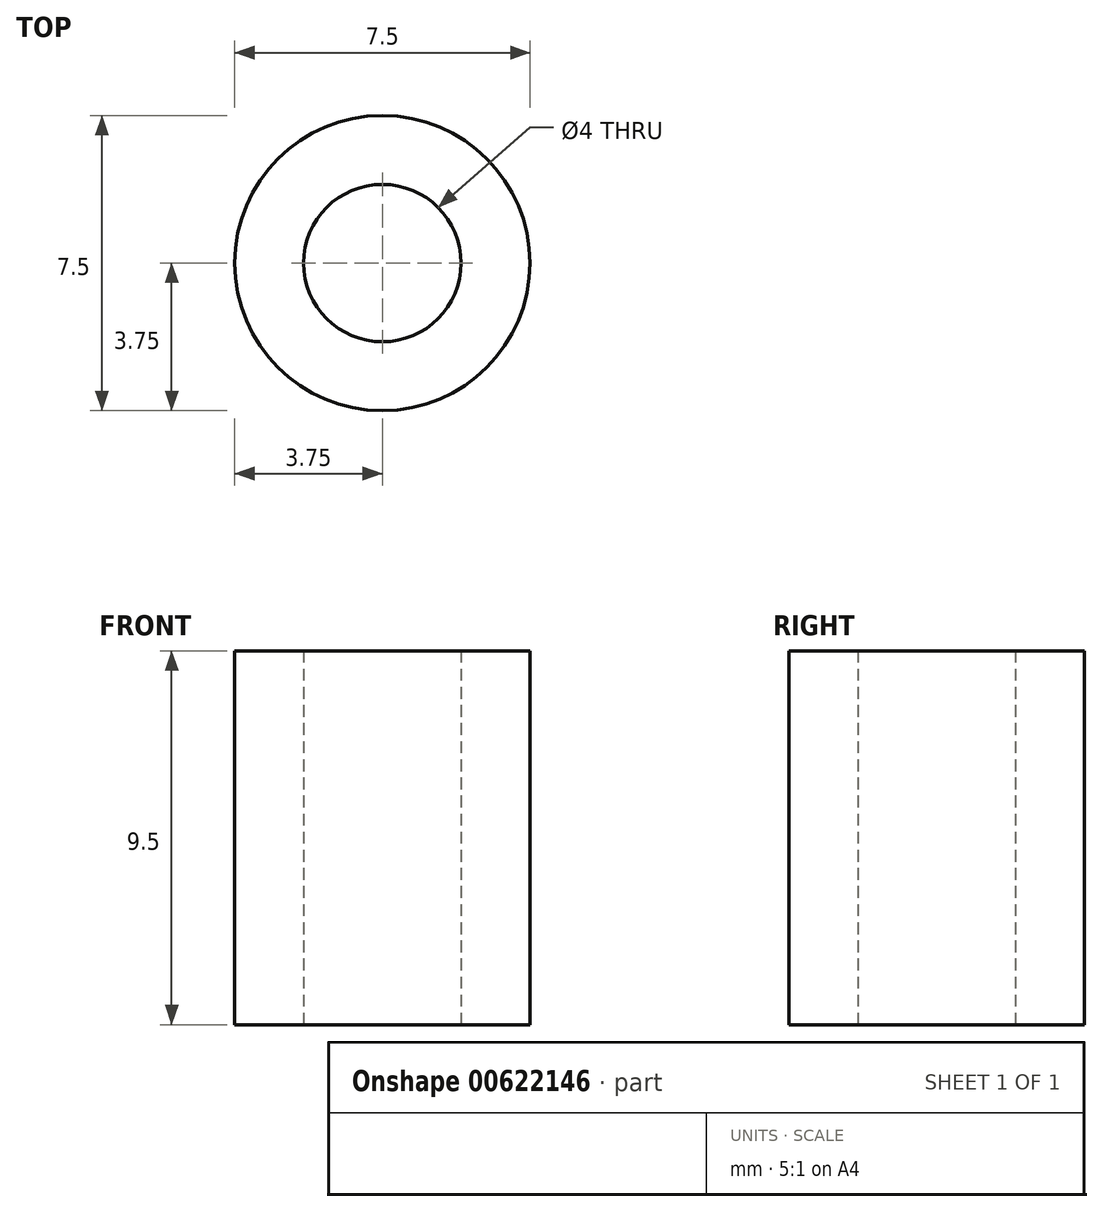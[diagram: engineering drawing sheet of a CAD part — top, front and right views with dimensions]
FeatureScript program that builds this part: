
annotation { "Feature Type Name" : "Feature", "Feature Type Description" : "" }
export const myFeature = defineFeature(function(context is Context, id is Id, definition is map)
    precondition{}
    {
        {
            var Q0;
            Q0=qCreatedBy(makeId("Top.planeOp"),FACE);
            var sketch = newSketch(context, id + "F0", { "sketchPlane" : qUnion([Q0])});
            skCircle(sketch, "E0", {"center": v(0, 0) * mm, "radius": 2 * mm});
            skCircle(sketch, "E1", {"center": v(0, 0) * mm, "radius": 3.75 * mm});
            skSolve(sketch);
        }
        {
            var Q0;
            Q0=makeQuery(id+"F0.imprint","IMPRINT",FACE,{"disambiguationData":[TD([[makeQuery(id+"F0.imprint","IMPRINT",EDGE,{"derivedFrom":sQuery(id+"F0.wireOp",EDGE,"E0")}),-1.0]])]});
            extrude(context, id + "F1", {"entities" : qUnion([Q0]), "depth" : 9.5 * mm, "offsetDistance" : 25 * mm});
        }
    });
